FCSTD DOCUMENT  (FreeCAD 0.18.4R)
Label: 17poly
License: All rights reserved
LicenseURL: http://en.wikipedia.org/wiki/All_rights_reserved
objects: Part::Part2DObjectPython×57
note: 57 computed .brp shape members not serialized (recipe doc carries the construction recipe); baked Part::Feature solids carry a one-line shape summary decoded from their .brp

FEATURE [Part::Part2DObjectPython] Polygon  # Draft 2D object (typed FeaturePython)
  ChamferSize = 0
  DrawMode = 0
  FacesNumber = 17
  FilletRadius = 0
  MakeFace = false
  Radius = 47.5
FEATURE [Part::Part2DObjectPython] Line  label="Line000"  # Draft 2D object (typed FeaturePython)
  ChamferSize = 0
  Closed = false
  End = (0,0,0)
  FilletRadius = 0
  Length = 46.6912
  MakeFace = false
  Points = (2) [(-20.8121,41.7963,0),(0,0,0)]
  Start = (-20.8121,41.7963,0)
  Subdivisions = 0
FEATURE [Part::Part2DObjectPython] Line001  # Draft 2D object (typed FeaturePython)
  ChamferSize = 0
  Closed = false
  End = (0,0,0)
  FilletRadius = 0
  Length = 46.6912
  MakeFace = false
  Points = (2) [(-4.30812,46.492,0),(0,0,0)]
  Start = (-4.30812,46.492,0)
  Subdivisions = 0
FEATURE [Part::Part2DObjectPython] Line002  # Draft 2D object (typed FeaturePython)
  ChamferSize = 0
  Closed = false
  End = (0,0,0)
  FilletRadius = 0
  Length = 46.6912
  MakeFace = false
  Points = (2) [(12.7777,44.9088,0),(0,0,0)]
  Start = (12.7777,44.9088,0)
  Subdivisions = 0
FEATURE [Part::Part2DObjectPython] Line003  # Draft 2D object (typed FeaturePython)
  ChamferSize = 0
  Closed = false
  End = (-3.6e-15,0,0)
  FilletRadius = 0
  Length = 46.6912
  MakeFace = false
  Points = (2) [(28.1377,37.2604,0),(-3.55271e-15,1.0877e-31,0)]
  Start = (28.1377,37.2604,0)
  Subdivisions = 0
FEATURE [Part::Part2DObjectPython] Line004  # Draft 2D object (typed FeaturePython)
  ChamferSize = 0
  Closed = false
  End = (0,0,0)
  FilletRadius = 0
  Length = 46.6912
  MakeFace = false
  Points = (2) [(39.6977,24.5798,0),(0,0,0)]
  Start = (39.6977,24.5798,0)
  Subdivisions = 0
FEATURE [Part::Part2DObjectPython] Line005  # Draft 2D object (typed FeaturePython)
  ChamferSize = 0
  Closed = false
  End = (0,0,0)
  FilletRadius = 0
  Length = 46.6912
  MakeFace = false
  Points = (2) [(45.8962,8.57949,0),(0,0,0)]
  Start = (45.8962,8.57949,0)
  Subdivisions = 0
FEATURE [Part::Part2DObjectPython] Line006  # Draft 2D object (typed FeaturePython)
  ChamferSize = 0
  Closed = false
  End = (0,3.6e-15,0)
  FilletRadius = 0
  Length = 46.6912
  MakeFace = false
  Points = (2) [(-34.5052,31.4557,0),(1.0877e-31,3.55271e-15,0)]
  Start = (-34.5052,31.4557,0)
  Subdivisions = 0
FEATURE [Part::Part2DObjectPython] Line007  # Draft 2D object (typed FeaturePython)
  ChamferSize = 0
  Closed = false
  End = (0,0,0)
  FilletRadius = 0
  Length = 46.6912
  MakeFace = false
  Points = (2) [(-43.5383,16.8668,0),(0,0,0)]
  Start = (-43.5383,16.8668,0)
  Subdivisions = 0
FEATURE [Part::Part2DObjectPython] Line008  # Draft 2D object (typed FeaturePython)
  ChamferSize = 0
  Closed = false
  End = (0,0,0)
  FilletRadius = 0
  Length = 46.6912
  MakeFace = false
  Points = (2) [(-46.6912,-1.42951e-15,0),(1.20759e-47,3.9443e-31,0)]
  Start = (-46.6912,-2.9e-15,0)
  Subdivisions = 0
FEATURE [Part::Part2DObjectPython] Line009  # Draft 2D object (typed FeaturePython)
  ChamferSize = 0
  Closed = false
  End = (0,0,0)
  FilletRadius = 0
  Length = 46.6912
  MakeFace = false
  Points = (2) [(-43.5383,-16.8668,0),(0,0,0)]
  Start = (-43.5383,-16.8668,0)
  Subdivisions = 0
FEATURE [Part::Part2DObjectPython] Line010  # Draft 2D object (typed FeaturePython)
  ChamferSize = 0
  Closed = false
  End = (0,0,0)
  FilletRadius = 0
  Length = 46.6912
  MakeFace = false
  Points = (2) [(-34.5052,-31.4557,0),(0,0,0)]
  Start = (-34.5052,-31.4557,0)
  Subdivisions = 0
FEATURE [Part::Part2DObjectPython] Line011  # Draft 2D object (typed FeaturePython)
  ChamferSize = 0
  Closed = false
  End = (0,0,0)
  FilletRadius = 0
  Length = 46.6912
  MakeFace = false
  Points = (2) [(-20.8121,-41.7963,0),(0,0,0)]
  Start = (-20.8121,-41.7963,0)
  Subdivisions = 0
FEATURE [Part::Part2DObjectPython] Line012  # Draft 2D object (typed FeaturePython)
  ChamferSize = 0
  Closed = false
  End = (0,0,0)
  FilletRadius = 0
  Length = 46.6912
  MakeFace = false
  Points = (2) [(-4.30812,-46.492,0),(0,0,0)]
  Start = (-4.30812,-46.492,0)
  Subdivisions = 0
FEATURE [Part::Part2DObjectPython] Line013  # Draft 2D object (typed FeaturePython)
  ChamferSize = 0
  Closed = false
  End = (1.8e-15,-7.1e-15,0)
  FilletRadius = 0
  Length = 46.6912
  MakeFace = false
  Points = (2) [(12.7777,-44.9088,0),(1.77636e-15,-7.10543e-15,0)]
  Start = (12.7777,-44.9088,0)
  Subdivisions = 0
FEATURE [Part::Part2DObjectPython] Line014  # Draft 2D object (typed FeaturePython)
  ChamferSize = 0
  Closed = false
  End = (0,0,0)
  FilletRadius = 0
  Length = 46.6912
  MakeFace = false
  Points = (2) [(28.1377,-37.2604,0),(0,0,0)]
  Start = (28.1377,-37.2604,0)
  Subdivisions = 0
FEATURE [Part::Part2DObjectPython] Line015  # Draft 2D object (typed FeaturePython)
  ChamferSize = 0
  Closed = false
  End = (0,0,0)
  FilletRadius = 0
  Length = 46.6912
  MakeFace = false
  Points = (2) [(39.6977,-24.5798,0),(0,0,0)]
  Start = (39.6977,-24.5798,0)
  Subdivisions = 0
FEATURE [Part::Part2DObjectPython] Line016  # Draft 2D object (typed FeaturePython)
  ChamferSize = 0
  Closed = false
  End = (0,0,0)
  FilletRadius = 0
  Length = 46.6912
  MakeFace = false
  Points = (2) [(45.8962,-8.57949,0),(0,0,0)]
  Start = (45.8962,-8.57949,0)
  Subdivisions = 0
FEATURE [Part::Part2DObjectPython] Circle  label="Circle_R"  # Draft 2D object (typed FeaturePython)
  FirstAngle = 0
  LastAngle = 0
  MakeFace = false
  Radius = 20
FEATURE [Part::Part2DObjectPython] Line017  # Draft 2D object (typed FeaturePython)
  ChamferSize = 0
  Closed = false
  End = (-37.353,-6.98248,0)
  FilletRadius = 0
  Length = 38
  MakeFace = false
  Points = (2) [(0,0,0),(-37.353,-6.98248,0)]
  Start = (0,0,0)
  Subdivisions = 0
FEATURE [Part::Part2DObjectPython] Line018  # Draft 2D object (typed FeaturePython)
  ChamferSize = 0
  Closed = false
  End = (-37.353,6.98248,0)
  FilletRadius = 0
  Length = 38
  MakeFace = false
  Points = (2) [(0,0,0),(-37.353,6.98248,0)]
  Start = (0,0,0)
  Subdivisions = 0
FEATURE [Part::Part2DObjectPython] Line019  # Draft 2D object (typed FeaturePython)
  ChamferSize = 0
  Closed = false
  End = (-32.3083,20.0044,0)
  FilletRadius = 0
  Length = 38
  MakeFace = false
  Points = (2) [(0,0,0),(-32.3083,20.0044,0)]
  Start = (0,0,0)
  Subdivisions = 0
FEATURE [Part::Part2DObjectPython] Line020  # Draft 2D object (typed FeaturePython)
  ChamferSize = 0
  Closed = false
  End = (-22.9001,30.3247,0)
  FilletRadius = 0
  Length = 38
  MakeFace = false
  Points = (2) [(0,0,0),(-22.9001,30.3247,0)]
  Start = (0,0,0)
  Subdivisions = 0
FEATURE [Part::Part2DObjectPython] Line021  # Draft 2D object (typed FeaturePython)
  ChamferSize = 0
  Closed = false
  End = (-10.3992,36.5494,0)
  FilletRadius = 0
  Length = 38
  MakeFace = false
  Placement = pos=(-7.1e-15,-7.1e-15,0) rot=(0,0,1;0rad)
  Points = (2) [(0,0,0),(-10.3992,36.5494,0)]
  Start = (-7.1e-15,-7.1e-15,0)
  Subdivisions = 0
FEATURE [Part::Part2DObjectPython] Line022  # Draft 2D object (typed FeaturePython)
  ChamferSize = 0
  Closed = false
  End = (3.5062,37.8379,0)
  FilletRadius = 0
  Length = 38
  MakeFace = false
  Points = (2) [(0,0,0),(3.5062,37.8379,0)]
  Start = (0,0,0)
  Subdivisions = 0
FEATURE [Part::Part2DObjectPython] Line023  # Draft 2D object (typed FeaturePython)
  ChamferSize = 0
  Closed = false
  End = (16.9381,34.0162,0)
  FilletRadius = 0
  Length = 38
  MakeFace = false
  Points = (2) [(0,0,0),(16.9381,34.0162,0)]
  Start = (0,0,0)
  Subdivisions = 0
FEATURE [Part::Part2DObjectPython] Line024  # Draft 2D object (typed FeaturePython)
  ChamferSize = 0
  Closed = false
  End = (35.4339,13.7272,0)
  FilletRadius = 0
  Length = 38
  MakeFace = false
  Points = (2) [(0,0,0),(35.4339,13.7272,0)]
  Start = (0,0,0)
  Subdivisions = 0
FEATURE [Part::Part2DObjectPython] Line025  # Draft 2D object (typed FeaturePython)
  ChamferSize = 0
  Closed = false
  End = (28.0823,25.6004,0)
  FilletRadius = 0
  Length = 38
  MakeFace = false
  Points = (2) [(0,0,0),(28.0823,25.6004,0)]
  Start = (0,0,0)
  Subdivisions = 0
FEATURE [Part::Part2DObjectPython] Line026  # Draft 2D object (typed FeaturePython)
  ChamferSize = 0
  Closed = false
  End = (38,2.3e-15,0)
  FilletRadius = 0
  Length = 38
  MakeFace = false
  Points = (2) [(0,0,0),(38,1.16341e-15,0)]
  Start = (0,0,0)
  Subdivisions = 0
FEATURE [Part::Part2DObjectPython] Line027  # Draft 2D object (typed FeaturePython)
  ChamferSize = 0
  Closed = false
  End = (35.4339,-13.7272,0)
  FilletRadius = 0
  Length = 38
  MakeFace = false
  Points = (2) [(0,0,0),(35.4339,-13.7272,0)]
  Start = (0,0,0)
  Subdivisions = 0
FEATURE [Part::Part2DObjectPython] Line028  # Draft 2D object (typed FeaturePython)
  ChamferSize = 0
  Closed = false
  End = (28.0823,-25.6004,0)
  FilletRadius = 0
  Length = 38
  MakeFace = false
  Points = (2) [(0,0,0),(28.0823,-25.6004,0)]
  Start = (0,0,0)
  Subdivisions = 0
FEATURE [Part::Part2DObjectPython] Line029  # Draft 2D object (typed FeaturePython)
  ChamferSize = 0
  Closed = false
  End = (16.9381,-34.0162,0)
  FilletRadius = 0
  Length = 38
  MakeFace = false
  Points = (2) [(0,0,0),(16.9381,-34.0162,0)]
  Start = (0,0,0)
  Subdivisions = 0
FEATURE [Part::Part2DObjectPython] Line030  # Draft 2D object (typed FeaturePython)
  ChamferSize = 0
  Closed = false
  End = (3.5062,-37.8379,0)
  FilletRadius = 0
  Length = 38
  MakeFace = false
  Points = (2) [(0,0,0),(3.5062,-37.8379,0)]
  Start = (0,0,0)
  Subdivisions = 0
FEATURE [Part::Part2DObjectPython] Line031  # Draft 2D object (typed FeaturePython)
  ChamferSize = 0
  Closed = false
  End = (-10.3992,-36.5494,0)
  FilletRadius = 0
  Length = 38
  MakeFace = false
  Points = (2) [(0,0,0),(-10.3992,-36.5494,0)]
  Start = (0,0,0)
  Subdivisions = 0
FEATURE [Part::Part2DObjectPython] Line032  # Draft 2D object (typed FeaturePython)
  ChamferSize = 0
  Closed = false
  End = (-22.9001,-30.3247,0)
  FilletRadius = 0
  Length = 38
  MakeFace = false
  Points = (2) [(0,0,0),(-22.9001,-30.3247,0)]
  Start = (0,0,0)
  Subdivisions = 0
FEATURE [Part::Part2DObjectPython] Line033  # Draft 2D object (typed FeaturePython)
  ChamferSize = 0
  Closed = false
  End = (-32.3083,-20.0044,0)
  FilletRadius = 0
  Length = 38
  MakeFace = false
  Points = (2) [(0,0,0),(-32.3083,-20.0044,0)]
  Start = (0,0,0)
  Subdivisions = 0
FEATURE [Part::Part2DObjectPython] Circle001  # Draft 2D object (typed FeaturePython)
  FirstAngle = 0
  LastAngle = 0
  MakeFace = false
  Placement = pos=(-37.353,-6.98248,0) rot=(0,0,1;0rad)
  Radius = 1.5
FEATURE [Part::Part2DObjectPython] Circle002  # Draft 2D object (typed FeaturePython)
  FirstAngle = 0
  LastAngle = 0
  MakeFace = false
  Placement = pos=(-37.353,6.98248,0) rot=(0,0,1;0rad)
  Radius = 1.5
FEATURE [Part::Part2DObjectPython] Circle003  # Draft 2D object (typed FeaturePython)
  FirstAngle = 0
  LastAngle = 0
  MakeFace = false
  Placement = pos=(-32.3083,20.0044,0) rot=(0,0,1;0rad)
  Radius = 1.5
FEATURE [Part::Part2DObjectPython] Circle004  # Draft 2D object (typed FeaturePython)
  FirstAngle = 0
  LastAngle = 0
  MakeFace = false
  Placement = pos=(-22.9001,30.3247,0) rot=(0,0,1;0rad)
  Radius = 1.5
FEATURE [Part::Part2DObjectPython] Circle005  # Draft 2D object (typed FeaturePython)
  FirstAngle = 0
  LastAngle = 0
  MakeFace = false
  Placement = pos=(-10.3992,36.5494,0) rot=(0,0,1;0rad)
  Radius = 1.5
FEATURE [Part::Part2DObjectPython] Circle006  # Draft 2D object (typed FeaturePython)
  FirstAngle = 0
  LastAngle = 0
  MakeFace = false
  Placement = pos=(3.5062,37.8379,0) rot=(0,0,1;0rad)
  Radius = 1.5
FEATURE [Part::Part2DObjectPython] Circle007  # Draft 2D object (typed FeaturePython)
  FirstAngle = 0
  LastAngle = 0
  MakeFace = false
  Placement = pos=(16.9381,34.0162,0) rot=(0,0,1;0rad)
  Radius = 1.5
FEATURE [Part::Part2DObjectPython] Circle008  # Draft 2D object (typed FeaturePython)
  FirstAngle = 0
  LastAngle = 0
  MakeFace = false
  Placement = pos=(28.0823,25.6004,0) rot=(0,0,1;0rad)
  Radius = 1.5
FEATURE [Part::Part2DObjectPython] Circle009  # Draft 2D object (typed FeaturePython)
  FirstAngle = 0
  LastAngle = 0
  MakeFace = false
  Placement = pos=(35.4339,13.7272,0) rot=(0,0,1;0rad)
  Radius = 1.5
FEATURE [Part::Part2DObjectPython] Circle010  # Draft 2D object (typed FeaturePython)
  FirstAngle = 0
  LastAngle = 0
  MakeFace = false
  Placement = pos=(38,0,0) rot=(0,0,1;0rad)
  Radius = 1.5
FEATURE [Part::Part2DObjectPython] Circle011  # Draft 2D object (typed FeaturePython)
  FirstAngle = 0
  LastAngle = 0
  MakeFace = false
  Placement = pos=(35.4142,-13.7631,0) rot=(0,0,1;0rad)
  Radius = 1.5
FEATURE [Part::Part2DObjectPython] Circle012  # Draft 2D object (typed FeaturePython)
  FirstAngle = 0
  LastAngle = 0
  MakeFace = false
  Placement = pos=(28.0823,-25.6004,0) rot=(0,0,1;0rad)
  Radius = 1.5
FEATURE [Part::Part2DObjectPython] Circle013  # Draft 2D object (typed FeaturePython)
  FirstAngle = 0
  LastAngle = 0
  MakeFace = false
  Placement = pos=(16.9381,-34.0162,0) rot=(0,0,1;0rad)
  Radius = 1.5
FEATURE [Part::Part2DObjectPython] Circle014  # Draft 2D object (typed FeaturePython)
  FirstAngle = 0
  LastAngle = 0
  MakeFace = false
  Placement = pos=(3.5062,-37.8379,0) rot=(0,0,1;0rad)
  Radius = 1.5
FEATURE [Part::Part2DObjectPython] Circle015  # Draft 2D object (typed FeaturePython)
  FirstAngle = 0
  LastAngle = 0
  MakeFace = false
  Placement = pos=(-10.3992,-36.5494,0) rot=(0,0,1;0rad)
  Radius = 1.5
FEATURE [Part::Part2DObjectPython] Circle016  # Draft 2D object (typed FeaturePython)
  FirstAngle = 0
  LastAngle = 0
  MakeFace = false
  Placement = pos=(-22.9001,-30.3247,0) rot=(0,0,1;0rad)
  Radius = 1.5
FEATURE [Part::Part2DObjectPython] Circle017  # Draft 2D object (typed FeaturePython)
  FirstAngle = 0
  LastAngle = 0
  MakeFace = false
  Placement = pos=(-32.3083,-20.0044,0) rot=(0,0,1;0rad)
  Radius = 1.5
FEATURE [Part::Part2DObjectPython] Circle018  label="CenterHole"  # Draft 2D object (typed FeaturePython)
  FirstAngle = 0
  LastAngle = 0
  MakeFace = false
  Placement = pos=(-1.5e-14,-1.9e-14,0) rot=(0,0,1;0rad)
  Radius = 1
FEATURE [Part::Part2DObjectPython] Polygon001  label="Polygon10mm"  # Draft 2D object (typed FeaturePython)
  ChamferSize = 0
  DrawMode = 0
  FacesNumber = 17
  FilletRadius = 0
  MakeFace = false
  Radius = 10
FEATURE [Part::Part2DObjectPython] Polygon002  label="Polygon15mm"  # Draft 2D object (typed FeaturePython)
  ChamferSize = 0
  DrawMode = 0
  FacesNumber = 17
  FilletRadius = 0
  MakeFace = false
  Radius = 15
FEATURE [Part::Part2DObjectPython] Polygon003  # Draft 2D object (typed FeaturePython)
  ChamferSize = 0
  DrawMode = 0
  FacesNumber = 17
  FilletRadius = 0
  MakeFace = false
  Radius = 20
